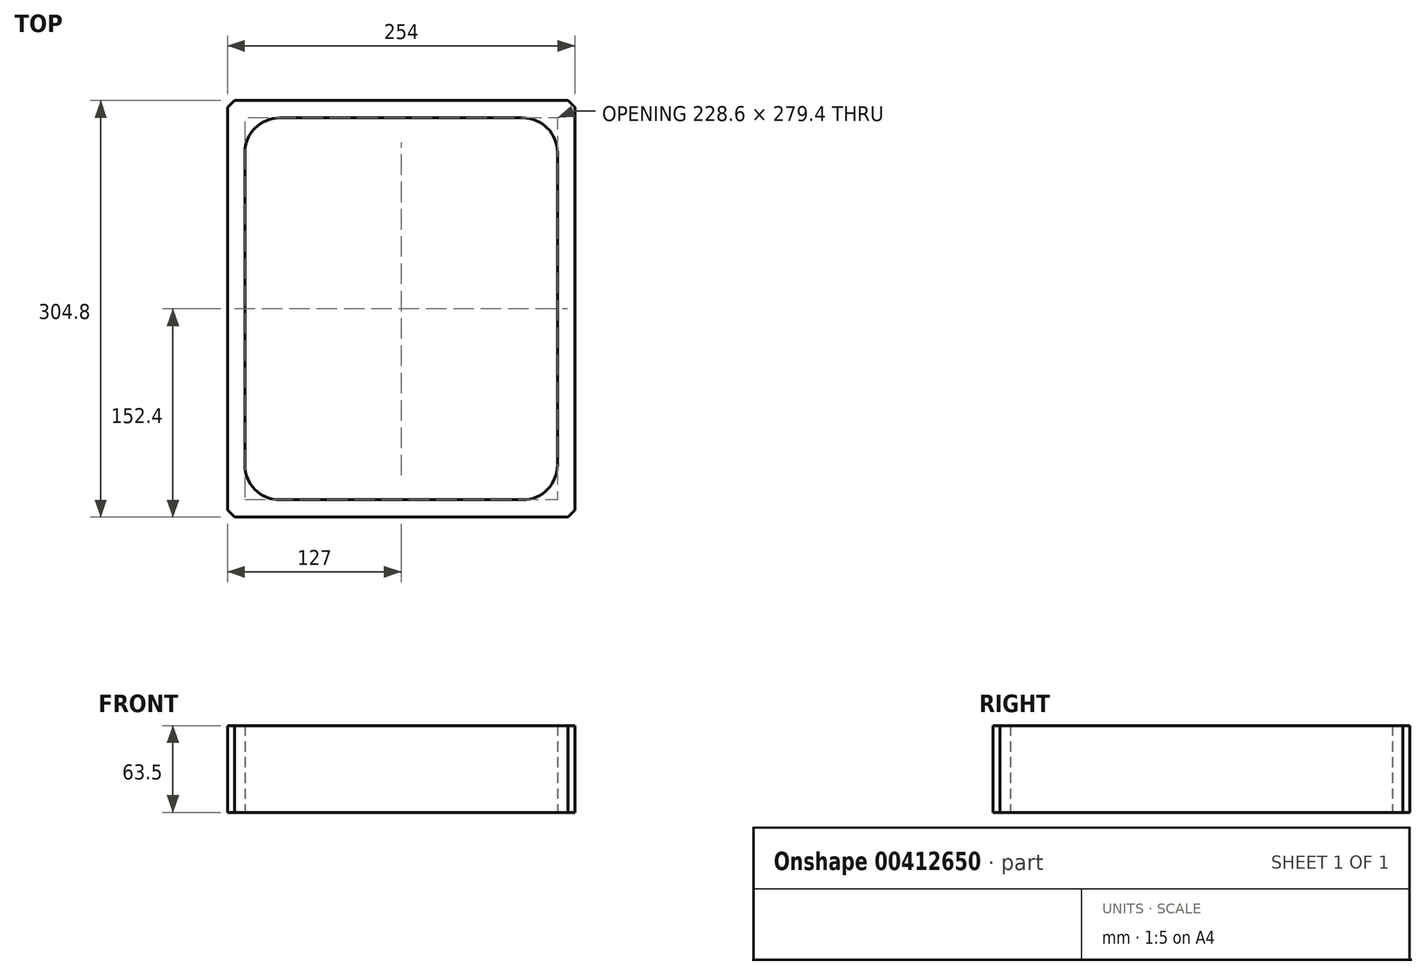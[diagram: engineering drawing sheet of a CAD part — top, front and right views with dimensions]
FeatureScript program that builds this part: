
annotation { "Feature Type Name" : "Feature", "Feature Type Description" : "" }
export const myFeature = defineFeature(function(context is Context, id is Id, definition is map)
    precondition{}
    {
        {
            var Q0;
            Q0=qCreatedBy(makeId("Top.planeOp"),FACE);
            var sketch = newSketch(context, id + "F0", { "sketchPlane" : qUnion([Q0])});
            skLineSegment(sketch, "E0.bottom", {"start": v(-127, 152.4) * mm, "end": v(127, 152.4) * mm});
            skLineSegment(sketch, "E0.top", {"start": v(-127, -152.4) * mm, "end": v(127, -152.4) * mm});
            skLineSegment(sketch, "E0.left", {"start": v(-127, 152.4) * mm, "end": v(-127, -152.4) * mm});
            skLineSegment(sketch, "E0.right", {"start": v(127, 152.4) * mm, "end": v(127, -152.4) * mm});
            skPoint(sketch, "E0.middle", {"position": v(0, 0) * mm});
            skLineSegment(sketch, "E1.0", {"start": v(-88.9, 139.7) * mm, "end": v(88.9, 139.7) * mm});
            skLineSegment(sketch, "E1.1", {"start": v(-114.3, 114.3) * mm, "end": v(-114.3, -114.3) * mm});
            skLineSegment(sketch, "E1.2", {"start": v(-88.9, -139.7) * mm, "end": v(88.9, -139.7) * mm});
            skLineSegment(sketch, "E1.3", {"start": v(114.3, 114.3) * mm, "end": v(114.3, -114.3) * mm});
            skPoint(sketch, "E2.visualSharp", {"position": v(-114.3, 139.7) * mm});
            skArc(sketch, "E2.filletArc", {"start": v(-88.9, 139.7) * mm, "mid": v(-106.86, 132.26) * mm, "end": v(-114.3, 114.3) * mm});
            skPoint(sketch, "E3.visualSharp", {"position": v(114.3, 139.7) * mm});
            skArc(sketch, "E3.filletArc", {"start": v(114.3, 114.3) * mm, "mid": v(106.86, 132.26) * mm, "end": v(88.9, 139.7) * mm});
            skPoint(sketch, "E4.visualSharp", {"position": v(114.3, -139.7) * mm});
            skArc(sketch, "E4.filletArc", {"start": v(88.9, -139.7) * mm, "mid": v(106.86, -132.26) * mm, "end": v(114.3, -114.3) * mm});
            skPoint(sketch, "E5.visualSharp", {"position": v(-114.3, -139.7) * mm});
            skArc(sketch, "E5.filletArc", {"start": v(-114.3, -114.3) * mm, "mid": v(-106.86, -132.26) * mm, "end": v(-88.9, -139.7) * mm});
            skSolve(sketch);
        }
        {
            var Q0;
            Q0=makeQuery(id+"F0.imprint","IMPRINT",FACE,{"disambiguationData":[TD([[makeQuery(id+"F0.imprint","IMPRINT",EDGE,{"derivedFrom":sQuery(id+"F0.wireOp",EDGE,"E0.bottom")}),-1.0]])]});
            extrude(context, id + "F1", {"entities" : qUnion([Q0]), "depth" : 63.5 * mm});
        }
        {
            var Q0;
            Q0=makeQuery(id+"F1.opExtrude","SWEPT_EDGE",EDGE,{"disambiguationData":[OSD([sQuery(id+"F0.wireOp",EDGE,"E0.bottom"),sQuery(id+"F0.wireOp",EDGE,"E0.left")])]});
            var Q1;
            Q1=makeQuery(id+"F1.opExtrude","SWEPT_EDGE",EDGE,{"disambiguationData":[OSD([sQuery(id+"F0.wireOp",EDGE,"E0.bottom"),sQuery(id+"F0.wireOp",EDGE,"E0.right")])]});
            var Q2;
            Q2=makeQuery(id+"F1.opExtrude","SWEPT_EDGE",EDGE,{"disambiguationData":[OSD([sQuery(id+"F0.wireOp",EDGE,"E0.top"),sQuery(id+"F0.wireOp",EDGE,"E0.right")])]});
            var Q3;
            Q3=makeQuery(id+"F1.opExtrude","SWEPT_EDGE",EDGE,{"disambiguationData":[OSD([sQuery(id+"F0.wireOp",EDGE,"E0.top"),sQuery(id+"F0.wireOp",EDGE,"E0.left")])]});
            chamfer(context, id + "F2", {"entities" : qUnion([Q0, Q1, Q2, Q3]), "width" : 5.08 * mm, "tangentPropagation" : true});
        }
    });
